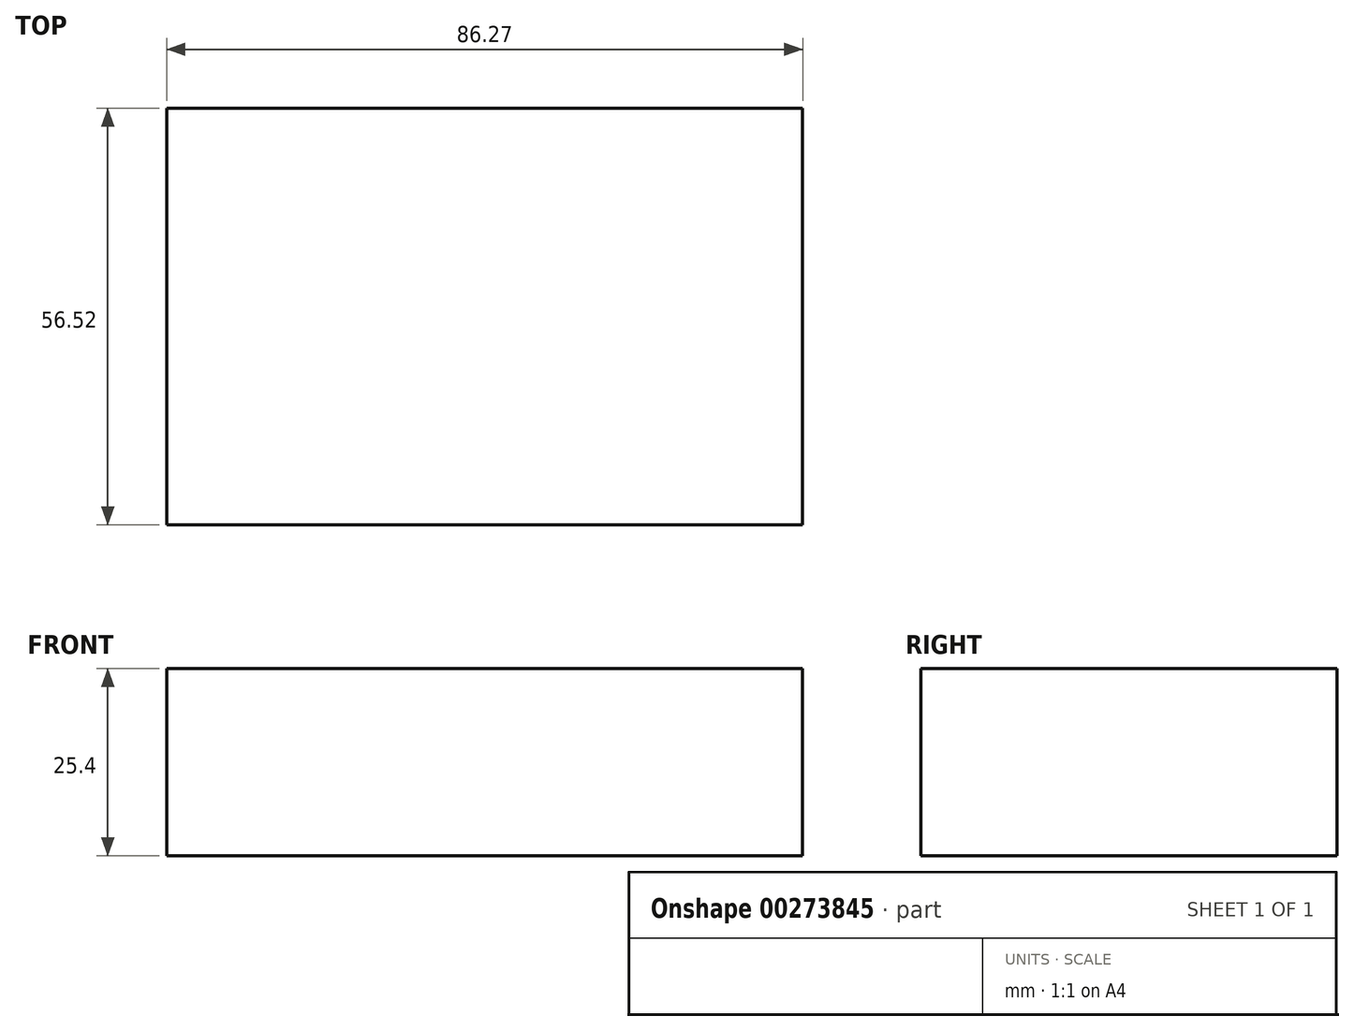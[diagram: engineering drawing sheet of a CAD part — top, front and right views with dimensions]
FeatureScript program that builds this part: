
annotation { "Feature Type Name" : "Feature", "Feature Type Description" : "" }
export const myFeature = defineFeature(function(context is Context, id is Id, definition is map)
    precondition{}
    {
        {
            var Q0;
            Q0=qCreatedBy(makeId("Top.planeOp"),FACE);
            var sketch = newSketch(context, id + "F0", { "sketchPlane" : qUnion([Q0])});
            skLineSegment(sketch, "E0.bottom", {"start": v(13.39, 4.2) * mm, "end": v(-72.88, 4.2) * mm});
            skLineSegment(sketch, "E0.top", {"start": v(13.39, 60.7) * mm, "end": v(-72.88, 60.7) * mm});
            skLineSegment(sketch, "E0.left", {"start": v(13.39, 4.2) * mm, "end": v(13.39, 60.7) * mm});
            skLineSegment(sketch, "E0.right", {"start": v(-72.88, 4.2) * mm, "end": v(-72.88, 60.7) * mm});
            skPoint(sketch, "E0.middle", {"position": v(-29.75, 32.45) * mm});
            skSolve(sketch);
        }
        {
            var Q0;
            Q0=makeQuery(id+"F0.imprint","IMPRINT",FACE,{"disambiguationData":[TD([[makeQuery(id+"F0.imprint","IMPRINT",EDGE,{"derivedFrom":sQuery(id+"F0.wireOp",EDGE,"E0.bottom")}),-1.0]])]});
            extrude(context, id + "F1", {"entities" : qUnion([Q0]), "oppositeDirection" : true, "depth" : 25.4 * mm});
        }
    });
